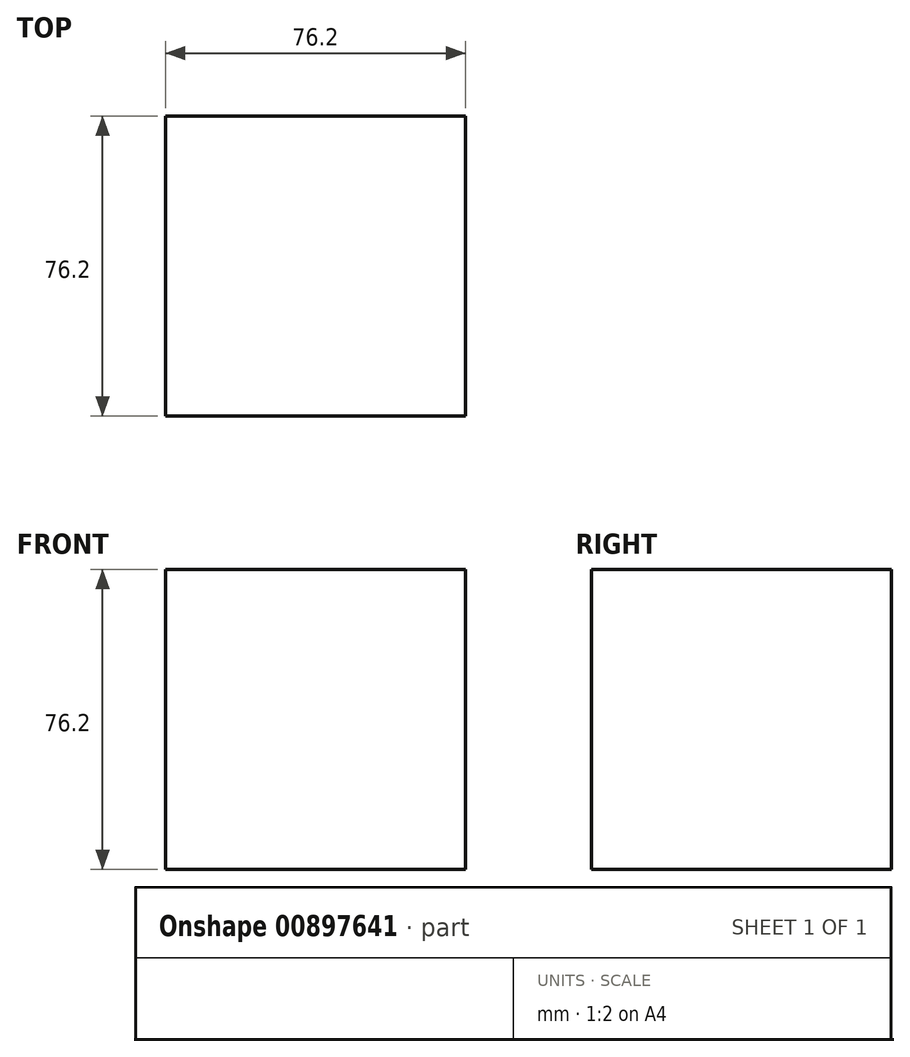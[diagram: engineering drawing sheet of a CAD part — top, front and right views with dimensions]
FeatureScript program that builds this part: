
annotation { "Feature Type Name" : "Feature", "Feature Type Description" : "" }
export const myFeature = defineFeature(function(context is Context, id is Id, definition is map)
    precondition{}
    {
        {
            var Q0;
            Q0=qCreatedBy(makeId("Front.planeOp"),FACE);
            var sketch = newSketch(context, id + "F0", { "sketchPlane" : qUnion([Q0])});
            skLineSegment(sketch, "E0.bottom", {"start": v(-42.05, 51.15) * mm, "end": v(34.15, 51.15) * mm});
            skLineSegment(sketch, "E0.top", {"start": v(-42.05, -25.05) * mm, "end": v(34.15, -25.05) * mm});
            skLineSegment(sketch, "E0.left", {"start": v(-42.05, 51.15) * mm, "end": v(-42.05, -25.05) * mm});
            skLineSegment(sketch, "E0.right", {"start": v(34.15, 51.15) * mm, "end": v(34.15, -25.05) * mm});
            skSolve(sketch);
        }
        {
            var Q0;
            Q0=makeQuery(id+"F0.imprint","IMPRINT",FACE,{"disambiguationData":[TD([[makeQuery(id+"F0.imprint","IMPRINT",EDGE,{"derivedFrom":sQuery(id+"F0.wireOp",EDGE,"E0.bottom")}),-1.0]])]});
            extrude(context, id + "F1", {"entities" : qUnion([Q0]), "depth" : 76.2 * mm, "offsetDistance" : 25.4 * mm});
        }
    });
